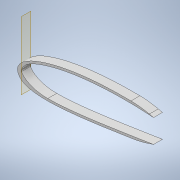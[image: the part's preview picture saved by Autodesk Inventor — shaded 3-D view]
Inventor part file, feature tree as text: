
AUTODESK INVENTOR PART (.ipt)
format: ipt  version: 2022.1 (Build 261234020, 234B)  size: 523,776 bytes
history: native  units: mm
features: sketch x6, extrude x5, thicken_offset x4, projected_geometry x2, shell x1, plane x1, other x1, fillet x1
ambient origin geometry x8: Origin, YZ Plane, XZ Plane, XY Plane, X Axis, Y Axis, Z Axis, Center Point
bodies: Solid1 (feature_tree)
feature tree (21):
  extrude  "Extrusion1"  Depth=3.0mm
  shell  "Shell1"  Thickness=1.0mm
  thicken_offset  "Thicken1"
  extrude  "Extrusion27"  TaperAngle=0.0deg  [1 undecoded]
  thicken_offset  "Thicken3"
  extrude  "Extrusion29"  Depth=30.0mm
  plane  "Work Plane5"
  other  "Bend Part2"
  thicken_offset  "Thicken5"
  extrude  "Extrusion31"  Depth=10.0mm TaperAngle=0.0deg
  thicken_offset  "Thicken6"
  extrude  "Extrusion32"  Depth=1.0mm
  fillet  "Fillet9"  Radius=1.0mm
  sketch  "Sketch3"  dims[d0=10.0mm d1=0.0mm d2=3.0mm d159=1.0mm d160=2.0mm]
  sketch  "Sketch48"  dims[d236=190.0mm d237=0.0mm d238=0.0mm]
  sketch  "Sketch55"  dims[d249=2.0mm d250=1.0mm d254=30.0mm]
  projected_geometry  "Projected Loop32"
  sketch  "Sketch57"  dims[d255=8.0mm d256=10.0mm d257=0.0mm]
  sketch  "Sketch59"  dims[d262=10.0mm d263=2.094395mm d264=1.0mm d265=1.0mm]
  sketch  "Sketch60"  dims[d272=150.0mm d273=100.0mm d274=0.0mm d282=2.5mm d283=2.5mm d284=10.0mm d285=0.0mm d286=100.0mm]
  projected_geometry  "Projected Loop35"
note: 1 required parameter value undecoded (feature->parameter linkage not recoverable at this tier; creation-order binding heuristic only, values carry confidence <= 0.55)
